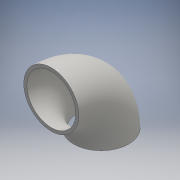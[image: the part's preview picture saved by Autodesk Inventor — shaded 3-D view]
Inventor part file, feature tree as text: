
AUTODESK INVENTOR PART (.ipt)
format: ipt  version: 2016 (Build 200138000, 138)  size: 159,744 bytes
history: native  units: mm
features: sweep x1, sketch x1
ambient origin geometry x8: Origin, YZ Plane, XZ Plane, XY Plane, X Axis, Y Axis, Z Axis, Center Point
bodies: Body1 (feature_tree)
feature tree (2):
  sweep  "Sweep6"
  sketch  "Sketch4"  dims[d23=229.0mm d27=168.0mm d28=9.57mm d29=0.0mm d30=0.0mm]
